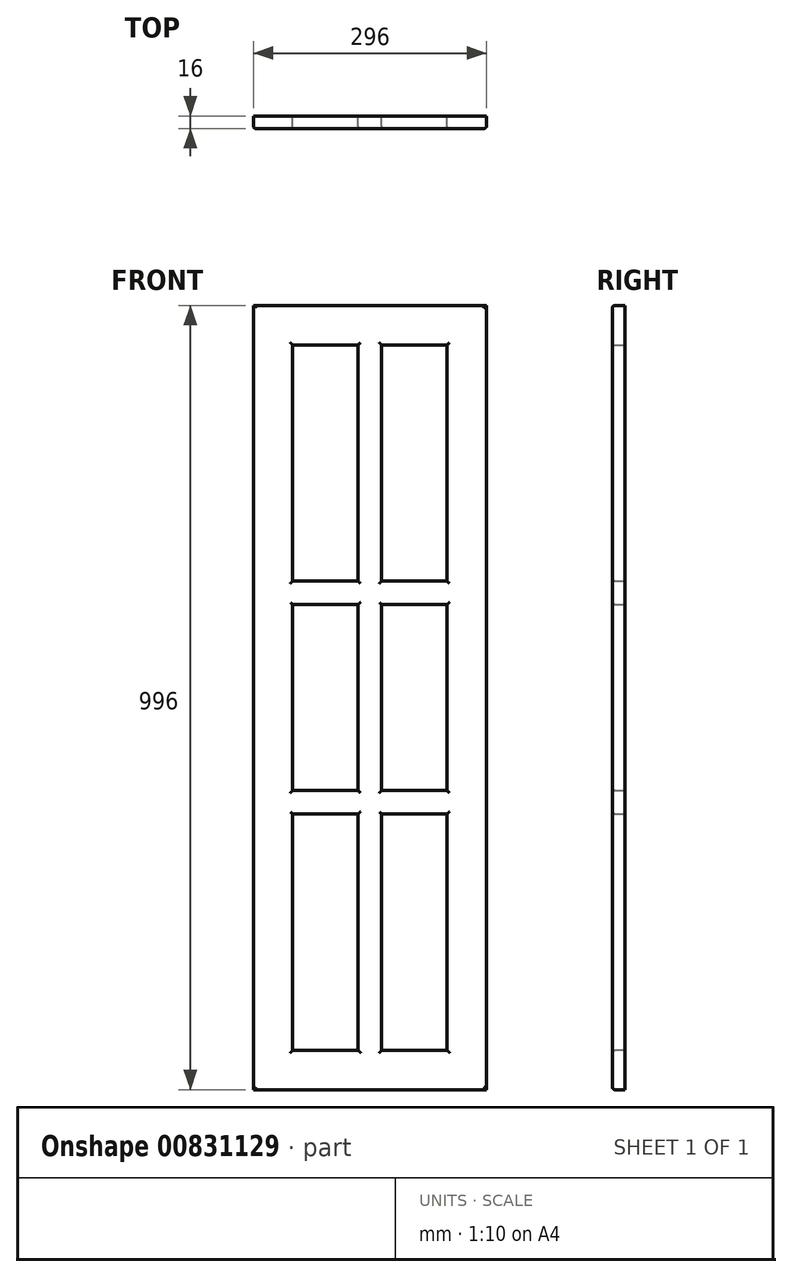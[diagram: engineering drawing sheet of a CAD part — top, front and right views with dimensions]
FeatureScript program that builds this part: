
annotation { "Feature Type Name" : "Feature", "Feature Type Description" : "" }
export const myFeature = defineFeature(function(context is Context, id is Id, definition is map)
    precondition{}
    {
        {
            var Q0;
            Q0=qCreatedBy(makeId("Front.planeOp"),FACE);
            var sketch = newSketch(context, id + "F0", { "sketchPlane" : qUnion([Q0])});
            skLineSegment(sketch, "E0.bottom", {"start": v(0, 0) * mm, "end": v(28.85, 0) * mm});
            skLineSegment(sketch, "E0.top", {"start": v(0, 37.88) * mm, "end": v(28.85, 37.88) * mm});
            skLineSegment(sketch, "E0.left", {"start": v(0, 0) * mm, "end": v(0, 37.88) * mm});
            skLineSegment(sketch, "E0.right", {"start": v(28.85, 0) * mm, "end": v(28.85, 37.88) * mm});
            skSolve(sketch);
        }
        {
            var Q0;
            Q0=makeQuery(id+"F0.imprint","IMPRINT",FACE,{"disambiguationData":[TD([[makeQuery(id+"F0.imprint","IMPRINT",EDGE,{"derivedFrom":sQuery(id+"F0.wireOp",EDGE,"E0.bottom")}),1.0]])]});
            extrude(context, id + "F1", {"entities" : qUnion([Q0]), "depth" : 16 * mm, "offsetDistance" : 25.4 * mm});
        }
        {
            var Q0;
            Q0=makeQuery(id+"F1.opExtrude","SWEPT_FACE",FACE,{"disambiguationData":[OSD([sQuery(id+"F0.wireOp",EDGE,"E0.left")])]});
            extrude(context, id + "F2", {"entities" : qUnion([Q0]), "operationType" : NewBodyOperationType.ADD, "oppositeDirection" : true, "depth" : 296 * mm, "offsetDistance" : 25.4 * mm});
        }
        {
            var Q0;
            {var subQ0=sQuery(id+"F0.wireOp",EDGE,"E0.bottom");Q0=makeQuery(id+"F2.boolean.opBoolean","MERGE",FACE,{"derivedFrom":[makeQuery(id+"F1.opExtrude","SWEPT_FACE",FACE,{"disambiguationData":[OSD([subQ0])]}),makeQuery(id+"F2.opExtrude","SWEPT_FACE",FACE,{"disambiguationData":[OSD([subQ0,sQuery(id+"F0.wireOp",EDGE,"E0.left")])]})]});}
            extrude(context, id + "F3", {"entities" : qUnion([Q0]), "operationType" : NewBodyOperationType.ADD, "oppositeDirection" : true, "depth" : 996 * mm, "offsetDistance" : 25 * mm});
        }
        {
            var Q0;
            {var subQ0=sQuery(id+"F0.wireOp",EDGE,"E0.left");var subQ1=sQuery(id+"F0.wireOp",EDGE,"E0.bottom");Q0=makeQuery(id+"F3.boolean.opBoolean","MERGE",FACE,{"derivedFrom":[makeQuery(id+"F2.boolean.opBoolean","MERGE",FACE,{"derivedFrom":[makeQuery(id+"F1.opExtrude","CAP_FACE",FACE,{"disambiguationData":[OSD([subQ1,sQuery(id+"F0.wireOp",EDGE,"E0.top"),subQ0,sQuery(id+"F0.wireOp",EDGE,"E0.right")])],"isStart":false}),makeQuery(id+"F2.opExtrude","SWEPT_FACE",FACE,{"disambiguationData":[OSD([subQ0]),TDD([makeQuery(id+"F1.opExtrude","CAP_EDGE",EDGE,{"disambiguationData":[OSD([subQ0])],"isStart":false})])]})]}),makeQuery(id+"F3.opExtrude","SWEPT_FACE",FACE,{"disambiguationData":[OSD([subQ1,subQ0]),TDD([makeQuery(id+"F2.boolean.opBoolean","MERGE",EDGE,{"derivedFrom":[makeQuery(id+"F1.opExtrude","CAP_EDGE",EDGE,{"disambiguationData":[OSD([subQ1])],"isStart":false}),makeQuery(id+"F2.opExtrude","SWEPT_EDGE",EDGE,{"disambiguationData":[OSD([subQ1,subQ0]),TDD([makeQuery(id+"F1.opExtrude","CAP_VERTEX",VERTEX,{"disambiguationData":[OSD([subQ1,subQ0])],"isStart":false})])]})]})])]})]});}
            var sketch = newSketch(context, id + "F4", { "sketchPlane" : qUnion([Q0])});
            skLineSegment(sketch, "E1.bottom", {"start": v(48.4, 906.79) * mm, "end": v(248.24, 906.79) * mm});
            skLineSegment(sketch, "E1.top", {"start": v(48.4, 105.66) * mm, "end": v(248.24, 105.66) * mm});
            skLineSegment(sketch, "E1.left", {"start": v(48.4, 906.79) * mm, "end": v(48.4, 105.66) * mm});
            skLineSegment(sketch, "E1.right", {"start": v(248.24, 906.79) * mm, "end": v(248.24, 105.66) * mm});
            skSolve(sketch);
        }
        {
            var Q0;
            Q0=makeQuery(id+"F4.imprint","IMPRINT",FACE,{"disambiguationData":[TD([[makeQuery(id+"F4.imprint","IMPRINT",EDGE,{"derivedFrom":sQuery(id+"F4.wireOp",EDGE,"E1.bottom")}),-1.0]])]});
            extrude(context, id + "F5", {"entities" : qUnion([Q0]), "operationType" : NewBodyOperationType.REMOVE, "oppositeDirection" : true, "depth" : 5 * mm, "offsetDistance" : 25 * mm});
        }
        {
            var Q0;
            Q0=makeQuery(id+"F5.boolean.opBoolean","COPY",FACE,{"derivedFrom":makeQuery(id+"F5.opExtrude","SWEPT_FACE",FACE,{"disambiguationData":[OSD([sQuery(id+"F4.wireOp",EDGE,"E1.bottom")])]})});
            extrude(context, id + "F6", {"entities" : qUnion([Q0]), "operationType" : NewBodyOperationType.REMOVE, "oppositeDirection" : true, "depth" : 39.2 * mm, "offsetDistance" : 25 * mm});
        }
        {
            var Q0;
            {var subQ0=sQuery(id+"F4.wireOp",EDGE,"E1.right");Q0=makeQuery(id+"F6.boolean.opBoolean","MERGE",FACE,{"derivedFrom":[makeQuery(id+"F5.boolean.opBoolean","COPY",FACE,{"derivedFrom":makeQuery(id+"F5.opExtrude","SWEPT_FACE",FACE,{"disambiguationData":[OSD([subQ0])]})}),makeQuery(id+"F6.opExtrude","SWEPT_FACE",FACE,{"disambiguationData":[OSD([sQuery(id+"F4.wireOp",EDGE,"E1.bottom"),subQ0])]})]});}
            extrude(context, id + "F7", {"entities" : qUnion([Q0]), "operationType" : NewBodyOperationType.ADD, "depth" : 2.24 * mm, "offsetDistance" : 25 * mm});
        }
        {
            var Q0;
            Q0=makeQuery(id+"F5.boolean.opBoolean","COPY",FACE,{"derivedFrom":makeQuery(id+"F5.opExtrude","SWEPT_FACE",FACE,{"disambiguationData":[OSD([sQuery(id+"F4.wireOp",EDGE,"E1.top")])]})});
            extrude(context, id + "F8", {"entities" : qUnion([Q0]), "operationType" : NewBodyOperationType.REMOVE, "oppositeDirection" : true, "depth" : 55.66 * mm, "offsetDistance" : 25 * mm});
        }
        {
            var Q0;
            {var subQ0=sQuery(id+"F4.wireOp",EDGE,"E1.left");Q0=makeQuery(id+"F8.boolean.opBoolean","MERGE",FACE,{"derivedFrom":[makeQuery(id+"F6.boolean.opBoolean","MERGE",FACE,{"derivedFrom":[makeQuery(id+"F5.boolean.opBoolean","COPY",FACE,{"derivedFrom":makeQuery(id+"F5.opExtrude","SWEPT_FACE",FACE,{"disambiguationData":[OSD([subQ0])]})}),makeQuery(id+"F6.opExtrude","SWEPT_FACE",FACE,{"disambiguationData":[OSD([sQuery(id+"F4.wireOp",EDGE,"E1.bottom"),subQ0])]})]}),makeQuery(id+"F8.opExtrude","SWEPT_FACE",FACE,{"disambiguationData":[OSD([sQuery(id+"F4.wireOp",EDGE,"E1.top"),subQ0])]})]});}
            extrude(context, id + "F9", {"entities" : qUnion([Q0]), "operationType" : NewBodyOperationType.ADD, "depth" : 1.59 * mm, "offsetDistance" : 25 * mm});
        }
        {
            var Q0;
            {var subQ0=sQuery(id+"F4.wireOp",EDGE,"E1.top");var subQ1=sQuery(id+"F4.wireOp",EDGE,"E1.bottom");Q0=makeQuery(id+"F8.boolean.opBoolean","MERGE",FACE,{"derivedFrom":[makeQuery(id+"F6.boolean.opBoolean","MERGE",FACE,{"derivedFrom":[makeQuery(id+"F5.boolean.opBoolean","COPY",FACE,{"derivedFrom":makeQuery(id+"F5.opExtrude","CAP_FACE",FACE,{"disambiguationData":[OSD([subQ1,subQ0,sQuery(id+"F4.wireOp",EDGE,"E1.left"),sQuery(id+"F4.wireOp",EDGE,"E1.right")])],"isStart":false})}),makeQuery(id+"F6.opExtrude","SWEPT_FACE",FACE,{"disambiguationData":[OSD([subQ1]),TDD([makeQuery(id+"F5.boolean.opBoolean","COPY",EDGE,{"derivedFrom":makeQuery(id+"F5.opExtrude","CAP_EDGE",EDGE,{"disambiguationData":[OSD([subQ1])],"isStart":false})})])]})]}),makeQuery(id+"F8.opExtrude","SWEPT_FACE",FACE,{"disambiguationData":[OSD([subQ0]),TDD([makeQuery(id+"F5.boolean.opBoolean","COPY",EDGE,{"derivedFrom":makeQuery(id+"F5.opExtrude","CAP_EDGE",EDGE,{"disambiguationData":[OSD([subQ0])],"isStart":false})})])]})]});}
            var sketch = newSketch(context, id + "F10", { "sketchPlane" : qUnion([Q0])});
            skLineSegment(sketch, "E2.bottom", {"start": v(127.14, 946) * mm, "end": v(181.91, 946) * mm});
            skLineSegment(sketch, "E2.top", {"start": v(127.14, 50) * mm, "end": v(181.91, 50) * mm});
            skLineSegment(sketch, "E2.left", {"start": v(127.14, 946) * mm, "end": v(127.14, 50) * mm});
            skLineSegment(sketch, "E2.right", {"start": v(181.91, 946) * mm, "end": v(181.91, 50) * mm});
            skSolve(sketch);
        }
        {
            var Q0;
            Q0=makeQuery(id+"F10.imprint","IMPRINT",FACE,{"disambiguationData":[TD([[makeQuery(id+"F10.imprint","IMPRINT",EDGE,{"derivedFrom":sQuery(id+"F10.wireOp",EDGE,"E2.bottom")}),-1.0]])]});
            extrude(context, id + "F11", {"entities" : qUnion([Q0]), "operationType" : NewBodyOperationType.ADD, "depth" : 5 * mm, "offsetDistance" : 25 * mm});
        }
        {
            var Q0;
            Q0=makeQuery(id+"F11.opExtrude","SWEPT_FACE",FACE,{"disambiguationData":[OSD([sQuery(id+"F10.wireOp",EDGE,"E2.left")])]});
            extrude(context, id + "F12", {"entities" : qUnion([Q0]), "operationType" : NewBodyOperationType.REMOVE, "oppositeDirection" : true, "depth" : 5.86 * mm, "offsetDistance" : 25 * mm});
        }
        {
            var Q0;
            Q0=makeQuery(id+"F11.opExtrude","SWEPT_FACE",FACE,{"disambiguationData":[OSD([sQuery(id+"F10.wireOp",EDGE,"E2.right")])]});
            extrude(context, id + "F13", {"entities" : qUnion([Q0]), "operationType" : NewBodyOperationType.REMOVE, "oppositeDirection" : true, "depth" : 18.91 * mm, "offsetDistance" : 25 * mm});
        }
        {
            var Q0;
            {var subQ0=sQuery(id+"F10.wireOp",EDGE,"E2.left");var subQ1=sQuery(id+"F4.wireOp",EDGE,"E1.bottom");var subQ2=sQuery(id+"F4.wireOp",EDGE,"E1.top");var subQ3=sQuery(id+"F4.wireOp",EDGE,"E1.left");Q0=makeQuery(id+"F12.boolean.opBoolean","MERGE",FACE,{"derivedFrom":[makeQuery(id+"F11.boolean.opBoolean","SPLIT",FACE,{"disambiguationData":[TD([makeQuery(id+"F11.opExtrude","SWEPT_FACE",FACE,{"disambiguationData":[OSD([subQ0])]})])],"derivedFrom":makeQuery(id+"F8.boolean.opBoolean","MERGE",FACE,{"derivedFrom":[makeQuery(id+"F6.boolean.opBoolean","MERGE",FACE,{"derivedFrom":[makeQuery(id+"F5.boolean.opBoolean","COPY",FACE,{"derivedFrom":makeQuery(id+"F5.opExtrude","CAP_FACE",FACE,{"disambiguationData":[OSD([subQ1,subQ2,subQ3,sQuery(id+"F4.wireOp",EDGE,"E1.right")])],"isStart":false})}),makeQuery(id+"F6.opExtrude","SWEPT_FACE",FACE,{"disambiguationData":[OSD([subQ1]),TDD([makeQuery(id+"F5.boolean.opBoolean","COPY",EDGE,{"derivedFrom":makeQuery(id+"F5.opExtrude","CAP_EDGE",EDGE,{"disambiguationData":[OSD([subQ1])],"isStart":false})})])]})]}),makeQuery(id+"F8.opExtrude","SWEPT_FACE",FACE,{"disambiguationData":[OSD([subQ2]),TDD([makeQuery(id+"F5.boolean.opBoolean","COPY",EDGE,{"derivedFrom":makeQuery(id+"F5.opExtrude","CAP_EDGE",EDGE,{"disambiguationData":[OSD([subQ2])],"isStart":false})})])]})]})}),makeQuery(id+"F12.opExtrude","SWEPT_FACE",FACE,{"disambiguationData":[OSD([subQ0]),TDD([makeQuery(id+"F11.opExtrude","CAP_EDGE",EDGE,{"disambiguationData":[OSD([subQ0])],"isStart":true})])]})]});}
            var sketch = newSketch(context, id + "F14", { "sketchPlane" : qUnion([Q0])});
            skLineSegment(sketch, "E3.bottom", {"start": v(50, 870.78) * mm, "end": v(133, 870.78) * mm});
            skLineSegment(sketch, "E3.top", {"start": v(50, 835.83) * mm, "end": v(133, 835.83) * mm});
            skLineSegment(sketch, "E3.left", {"start": v(50, 870.78) * mm, "end": v(50, 835.83) * mm});
            skLineSegment(sketch, "E3.right", {"start": v(133, 870.78) * mm, "end": v(133, 835.83) * mm});
            skLineSegment(sketch, "E4.bottom", {"start": v(50, 539.3) * mm, "end": v(133, 539.3) * mm});
            skLineSegment(sketch, "E4.top", {"start": v(50, 484.02) * mm, "end": v(133, 484.02) * mm});
            skLineSegment(sketch, "E4.left", {"start": v(50, 539.3) * mm, "end": v(50, 484.02) * mm});
            skLineSegment(sketch, "E4.right", {"start": v(133, 539.3) * mm, "end": v(133, 484.02) * mm});
            skSolve(sketch);
        }
        {
            var Q0;
            {var subQ0=sQuery(id+"F10.wireOp",EDGE,"E2.right");var subQ1=sQuery(id+"F4.wireOp",EDGE,"E1.top");var subQ2=sQuery(id+"F4.wireOp",EDGE,"E1.right");var subQ3=sQuery(id+"F4.wireOp",EDGE,"E1.bottom");Q0=makeQuery(id+"F13.boolean.opBoolean","MERGE",FACE,{"derivedFrom":[makeQuery(id+"F11.boolean.opBoolean","SPLIT",FACE,{"disambiguationData":[TD([makeQuery(id+"F11.opExtrude","SWEPT_FACE",FACE,{"disambiguationData":[OSD([subQ0])]})])],"derivedFrom":makeQuery(id+"F8.boolean.opBoolean","MERGE",FACE,{"derivedFrom":[makeQuery(id+"F6.boolean.opBoolean","MERGE",FACE,{"derivedFrom":[makeQuery(id+"F5.boolean.opBoolean","COPY",FACE,{"derivedFrom":makeQuery(id+"F5.opExtrude","CAP_FACE",FACE,{"disambiguationData":[OSD([subQ3,subQ1,sQuery(id+"F4.wireOp",EDGE,"E1.left"),subQ2])],"isStart":false})}),makeQuery(id+"F6.opExtrude","SWEPT_FACE",FACE,{"disambiguationData":[OSD([subQ3]),TDD([makeQuery(id+"F5.boolean.opBoolean","COPY",EDGE,{"derivedFrom":makeQuery(id+"F5.opExtrude","CAP_EDGE",EDGE,{"disambiguationData":[OSD([subQ3])],"isStart":false})})])]})]}),makeQuery(id+"F8.opExtrude","SWEPT_FACE",FACE,{"disambiguationData":[OSD([subQ1]),TDD([makeQuery(id+"F5.boolean.opBoolean","COPY",EDGE,{"derivedFrom":makeQuery(id+"F5.opExtrude","CAP_EDGE",EDGE,{"disambiguationData":[OSD([subQ1])],"isStart":false})})])]})]})}),makeQuery(id+"F13.opExtrude","SWEPT_FACE",FACE,{"disambiguationData":[OSD([subQ0]),TDD([makeQuery(id+"F11.opExtrude","CAP_EDGE",EDGE,{"disambiguationData":[OSD([subQ0])],"isStart":true})])]})]});}
            var sketch = newSketch(context, id + "F15", { "sketchPlane" : qUnion([Q0])});
            skLineSegment(sketch, "E5.bottom", {"start": v(163, 876.14) * mm, "end": v(246, 876.14) * mm});
            skLineSegment(sketch, "E5.top", {"start": v(163, 831.26) * mm, "end": v(246, 831.26) * mm});
            skLineSegment(sketch, "E5.left", {"start": v(163, 876.14) * mm, "end": v(163, 831.26) * mm});
            skLineSegment(sketch, "E5.right", {"start": v(246, 876.14) * mm, "end": v(246, 831.26) * mm});
            skLineSegment(sketch, "E6.bottom", {"start": v(163, 602.8) * mm, "end": v(246, 602.8) * mm});
            skLineSegment(sketch, "E6.top", {"start": v(163, 550.28) * mm, "end": v(246, 550.28) * mm});
            skLineSegment(sketch, "E6.left", {"start": v(163, 602.8) * mm, "end": v(163, 550.28) * mm});
            skLineSegment(sketch, "E6.right", {"start": v(246, 602.8) * mm, "end": v(246, 550.28) * mm});
            skSolve(sketch);
        }
        {
            var Q0;
            Q0=makeQuery(id+"F14.imprint","IMPRINT",FACE,{"disambiguationData":[TD([[makeQuery(id+"F14.imprint","IMPRINT",EDGE,{"derivedFrom":sQuery(id+"F14.wireOp",EDGE,"E3.bottom")}),-1.0]])]});
            var Q1;
            Q1=makeQuery(id+"F15.imprint","IMPRINT",FACE,{"disambiguationData":[TD([[makeQuery(id+"F15.imprint","IMPRINT",EDGE,{"derivedFrom":sQuery(id+"F15.wireOp",EDGE,"E5.bottom")}),-1.0]])]});
            var Q2;
            Q2=makeQuery(id+"F15.imprint","IMPRINT",FACE,{"disambiguationData":[TD([[makeQuery(id+"F15.imprint","IMPRINT",EDGE,{"derivedFrom":sQuery(id+"F15.wireOp",EDGE,"E6.bottom")}),-1.0]])]});
            var Q3;
            Q3=makeQuery(id+"F14.imprint","IMPRINT",FACE,{"disambiguationData":[TD([[makeQuery(id+"F14.imprint","IMPRINT",EDGE,{"derivedFrom":sQuery(id+"F14.wireOp",EDGE,"E4.bottom")}),-1.0]])]});
            extrude(context, id + "F16", {"entities" : qUnion([Q0, Q1, Q2, Q3]), "operationType" : NewBodyOperationType.ADD, "depth" : 5 * mm, "offsetDistance" : 25 * mm});
        }
        {
            var Q0;
            Q0=makeQuery(id+"F16.opExtrude","SWEPT_FACE",FACE,{"disambiguationData":[OSD([sQuery(id+"F15.wireOp",EDGE,"E6.top")])]});
            var Q1;
            Q1=makeQuery(id+"F16.opExtrude","SWEPT_FACE",FACE,{"disambiguationData":[OSD([sQuery(id+"F14.wireOp",EDGE,"E4.top")])]});
            extrude(context, id + "F17", {"entities" : qUnion([Q0, Q1]), "operationType" : NewBodyOperationType.ADD, "depth" : 300 * mm, "offsetDistance" : 25 * mm});
        }
        {
            var Q0;
            Q0=makeQuery(id+"F16.opExtrude","SWEPT_FACE",FACE,{"disambiguationData":[OSD([sQuery(id+"F14.wireOp",EDGE,"E4.bottom")])]});
            var Q1;
            Q1=makeQuery(id+"F16.opExtrude","SWEPT_FACE",FACE,{"disambiguationData":[OSD([sQuery(id+"F15.wireOp",EDGE,"E6.bottom")])]});
            extrude(context, id + "F18", {"entities" : qUnion([Q0, Q1]), "operationType" : NewBodyOperationType.REMOVE, "oppositeDirection" : true, "depth" : 300 * mm, "offsetDistance" : 25 * mm});
        }
        {
            var Q0;
            Q0=makeQuery(id+"F16.opExtrude","SWEPT_FACE",FACE,{"disambiguationData":[OSD([sQuery(id+"F14.wireOp",EDGE,"E3.top")])]});
            extrude(context, id + "F19", {"entities" : qUnion([Q0]), "operationType" : NewBodyOperationType.ADD, "depth" : 324.8 * mm, "offsetDistance" : 25 * mm});
        }
        {
            var Q0;
            Q0=makeQuery(id+"F16.opExtrude","SWEPT_FACE",FACE,{"disambiguationData":[OSD([sQuery(id+"F14.wireOp",EDGE,"E3.bottom")])]});
            extrude(context, id + "F20", {"entities" : qUnion([Q0]), "operationType" : NewBodyOperationType.REMOVE, "oppositeDirection" : true, "depth" : 324.8 * mm, "offsetDistance" : 25 * mm});
        }
        {
            var Q0;
            Q0=makeQuery(id+"F18.boolean.opBoolean","COPY",FACE,{"derivedFrom":makeQuery(id+"F18.opExtrude","CAP_FACE",FACE,{"disambiguationData":[OSD([sQuery(id+"F14.wireOp",EDGE,"E4.bottom")])],"isStart":false})});
            extrude(context, id + "F21", {"entities" : qUnion([Q0]), "operationType" : NewBodyOperationType.ADD, "depth" : 250 * mm, "offsetDistance" : 25 * mm});
        }
        {
            var Q0;
            Q0=makeQuery(id+"F17.opExtrude","CAP_FACE",FACE,{"disambiguationData":[OSD([sQuery(id+"F14.wireOp",EDGE,"E4.top")])],"isStart":false});
            extrude(context, id + "F22", {"entities" : qUnion([Q0]), "operationType" : NewBodyOperationType.REMOVE, "oppositeDirection" : true, "depth" : 250 * mm, "offsetDistance" : 25 * mm});
        }
        {
            var Q0;
            Q0=makeQuery(id+"F20.boolean.opBoolean","COPY",FACE,{"derivedFrom":makeQuery(id+"F20.opExtrude","CAP_FACE",FACE,{"disambiguationData":[OSD([sQuery(id+"F14.wireOp",EDGE,"E3.bottom")])],"isStart":false})});
            extrude(context, id + "F23", {"entities" : qUnion([Q0]), "operationType" : NewBodyOperationType.ADD, "depth" : 100 * mm, "offsetDistance" : 25 * mm});
        }
        {
            var Q0;
            Q0=makeQuery(id+"F19.opExtrude","CAP_FACE",FACE,{"disambiguationData":[OSD([sQuery(id+"F14.wireOp",EDGE,"E3.top")])],"isStart":false});
            extrude(context, id + "F24", {"entities" : qUnion([Q0]), "operationType" : NewBodyOperationType.REMOVE, "oppositeDirection" : true, "depth" : 100 * mm, "offsetDistance" : 25 * mm});
        }
        {
            var Q0;
            Q0=makeQuery(id+"F23.opExtrude","CAP_FACE",FACE,{"disambiguationData":[OSD([sQuery(id+"F14.wireOp",EDGE,"E3.bottom")])],"isStart":false});
            extrude(context, id + "F25", {"entities" : qUnion([Q0]), "operationType" : NewBodyOperationType.ADD, "depth" : 50 * mm, "offsetDistance" : 25 * mm});
        }
        {
            var Q0;
            Q0=makeQuery(id+"F24.boolean.opBoolean","COPY",FACE,{"derivedFrom":makeQuery(id+"F24.opExtrude","CAP_FACE",FACE,{"disambiguationData":[OSD([sQuery(id+"F14.wireOp",EDGE,"E3.top")])],"isStart":false})});
            extrude(context, id + "F26", {"entities" : qUnion([Q0]), "operationType" : NewBodyOperationType.REMOVE, "oppositeDirection" : true, "depth" : 50 * mm, "offsetDistance" : 25 * mm});
        }
        {
            var Q0;
            Q0=makeQuery(id+"F22.boolean.opBoolean","COPY",FACE,{"derivedFrom":makeQuery(id+"F22.opExtrude","CAP_FACE",FACE,{"disambiguationData":[OSD([sQuery(id+"F14.wireOp",EDGE,"E4.top")])],"isStart":false})});
            extrude(context, id + "F27", {"entities" : qUnion([Q0]), "operationType" : NewBodyOperationType.ADD, "depth" : 134.02 * mm, "offsetDistance" : 25 * mm});
        }
        {
            var Q0;
            Q0=makeQuery(id+"F27.opExtrude","CAP_FACE",FACE,{"disambiguationData":[OSD([sQuery(id+"F14.wireOp",EDGE,"E4.top")])],"isStart":false});
            extrude(context, id + "F28", {"entities" : qUnion([Q0]), "operationType" : NewBodyOperationType.REMOVE, "oppositeDirection" : true, "depth" : 100 * mm, "offsetDistance" : 25 * mm});
        }
        {
            var Q0;
            Q0=makeQuery(id+"F26.boolean.opBoolean","COPY",FACE,{"derivedFrom":makeQuery(id+"F26.opExtrude","CAP_FACE",FACE,{"disambiguationData":[OSD([sQuery(id+"F14.wireOp",EDGE,"E3.top")])],"isStart":false})});
            extrude(context, id + "F29", {"entities" : qUnion([Q0]), "operationType" : NewBodyOperationType.ADD, "depth" : 100 * mm, "offsetDistance" : 25 * mm});
        }
        {
            var Q0;
            Q0=makeQuery(id+"F25.opExtrude","CAP_FACE",FACE,{"disambiguationData":[OSD([sQuery(id+"F14.wireOp",EDGE,"E3.bottom")])],"isStart":false});
            extrude(context, id + "F30", {"entities" : qUnion([Q0]), "operationType" : NewBodyOperationType.REMOVE, "oppositeDirection" : true, "depth" : 100 * mm, "offsetDistance" : 25 * mm});
        }
        {
            var Q0;
            Q0=makeQuery(id+"F30.boolean.opBoolean","COPY",FACE,{"derivedFrom":makeQuery(id+"F30.opExtrude","CAP_FACE",FACE,{"disambiguationData":[OSD([sQuery(id+"F14.wireOp",EDGE,"E3.bottom")])],"isStart":false})});
            extrude(context, id + "F31", {"entities" : qUnion([Q0]), "operationType" : NewBodyOperationType.ADD, "depth" : 50 * mm, "offsetDistance" : 25 * mm});
        }
        {
            var Q0;
            Q0=makeQuery(id+"F29.opExtrude","CAP_FACE",FACE,{"disambiguationData":[OSD([sQuery(id+"F14.wireOp",EDGE,"E3.top")])],"isStart":false});
            extrude(context, id + "F32", {"entities" : qUnion([Q0]), "operationType" : NewBodyOperationType.REMOVE, "oppositeDirection" : true, "depth" : 54.95 * mm, "offsetDistance" : 25 * mm});
        }
        {
            var Q0;
            Q0=makeQuery(id+"F28.boolean.opBoolean","COPY",FACE,{"derivedFrom":makeQuery(id+"F28.opExtrude","CAP_FACE",FACE,{"disambiguationData":[OSD([sQuery(id+"F14.wireOp",EDGE,"E4.top")])],"isStart":false})});
            extrude(context, id + "F33", {"entities" : qUnion([Q0]), "operationType" : NewBodyOperationType.ADD, "depth" : 50 * mm, "offsetDistance" : 25 * mm});
        }
        {
            var Q0;
            Q0=makeQuery(id+"F21.opExtrude","CAP_FACE",FACE,{"disambiguationData":[OSD([sQuery(id+"F14.wireOp",EDGE,"E4.bottom")])],"isStart":false});
            extrude(context, id + "F34", {"entities" : qUnion([Q0]), "operationType" : NewBodyOperationType.REMOVE, "oppositeDirection" : true, "depth" : 109.3 * mm, "offsetDistance" : 25 * mm});
        }
        {
            var Q0;
            Q0=makeQuery(id+"F16.opExtrude","SWEPT_FACE",FACE,{"disambiguationData":[OSD([sQuery(id+"F15.wireOp",EDGE,"E5.top")])]});
            extrude(context, id + "F35", {"entities" : qUnion([Q0]), "operationType" : NewBodyOperationType.REMOVE, "oppositeDirection" : true, "depth" : 14.88 * mm, "offsetDistance" : 25 * mm});
        }
        {
            var Q0;
            Q0=makeQuery(id+"F35.boolean.opBoolean","COPY",FACE,{"derivedFrom":makeQuery(id+"F35.opExtrude","CAP_FACE",FACE,{"disambiguationData":[OSD([sQuery(id+"F15.wireOp",EDGE,"E5.top")])],"isStart":false})});
            extrude(context, id + "F36", {"entities" : qUnion([Q0]), "operationType" : NewBodyOperationType.ADD, "depth" : 230.15 * mm, "offsetDistance" : 25 * mm});
        }
        {
            var Q0;
            Q0=makeQuery(id+"F16.opExtrude","SWEPT_FACE",FACE,{"disambiguationData":[OSD([sQuery(id+"F15.wireOp",EDGE,"E5.bottom")])]});
            extrude(context, id + "F37", {"entities" : qUnion([Q0]), "operationType" : NewBodyOperationType.REMOVE, "oppositeDirection" : true, "depth" : 230.15 * mm, "offsetDistance" : 25 * mm});
        }
        {
            var Q0;
            Q0=makeQuery(id+"F17.opExtrude","CAP_FACE",FACE,{"disambiguationData":[OSD([sQuery(id+"F15.wireOp",EDGE,"E6.top")])],"isStart":false});
            extrude(context, id + "F38", {"entities" : qUnion([Q0]), "operationType" : NewBodyOperationType.REMOVE, "oppositeDirection" : true, "depth" : 22.52 * mm, "offsetDistance" : 25 * mm});
        }
        {
            var Q0;
            Q0=makeQuery(id+"F18.boolean.opBoolean","COPY",FACE,{"derivedFrom":makeQuery(id+"F18.opExtrude","CAP_FACE",FACE,{"disambiguationData":[OSD([sQuery(id+"F15.wireOp",EDGE,"E6.bottom")])],"isStart":false})});
            extrude(context, id + "F39", {"entities" : qUnion([Q0]), "operationType" : NewBodyOperationType.ADD, "depth" : 77.2 * mm, "offsetDistance" : 25 * mm});
        }
        {
            var Q0;
            Q0=makeQuery(id+"F38.boolean.opBoolean","COPY",FACE,{"derivedFrom":makeQuery(id+"F38.opExtrude","CAP_FACE",FACE,{"disambiguationData":[OSD([sQuery(id+"F15.wireOp",EDGE,"E6.top")])],"isStart":false})});
            extrude(context, id + "F40", {"entities" : qUnion([Q0]), "operationType" : NewBodyOperationType.REMOVE, "oppositeDirection" : true, "depth" : 77.2 * mm, "offsetDistance" : 25 * mm});
        }
        {
            var Q0;
            {var subQ0=sQuery(id+"F14.wireOp",EDGE,"E3.bottom");var subQ1=makeQuery(id+"F16.opExtrude","CAP_EDGE",EDGE,{"disambiguationData":[OSD([subQ0])],"isStart":true});var subQ2=sQuery(id+"F10.wireOp",EDGE,"E2.left");var subQ3=sQuery(id+"F4.wireOp",EDGE,"E1.bottom");var subQ4=sQuery(id+"F4.wireOp",EDGE,"E1.left");var subQ5=sQuery(id+"F4.wireOp",EDGE,"E1.top");var subQ7=makeQuery(id+"F6.boolean.opBoolean","COPY",FACE,{"derivedFrom":makeQuery(id+"F6.opExtrude","CAP_FACE",FACE,{"disambiguationData":[OSD([subQ3])],"isStart":false})});Q0=makeQuery(id+"F30.boolean.opBoolean","MERGE",FACE,{"derivedFrom":[makeQuery(id+"F20.boolean.opBoolean","MERGE",FACE,{"derivedFrom":[makeQuery(id+"F16.boolean.opBoolean","SPLIT",FACE,{"disambiguationData":[TD([subQ7])],"derivedFrom":makeQuery(id+"F12.boolean.opBoolean","MERGE",FACE,{"derivedFrom":[makeQuery(id+"F11.boolean.opBoolean","SPLIT",FACE,{"disambiguationData":[TD([makeQuery(id+"F11.opExtrude","SWEPT_FACE",FACE,{"disambiguationData":[OSD([subQ2])]})])],"derivedFrom":makeQuery(id+"F8.boolean.opBoolean","MERGE",FACE,{"derivedFrom":[makeQuery(id+"F6.boolean.opBoolean","MERGE",FACE,{"derivedFrom":[makeQuery(id+"F5.boolean.opBoolean","COPY",FACE,{"derivedFrom":makeQuery(id+"F5.opExtrude","CAP_FACE",FACE,{"disambiguationData":[OSD([subQ3,subQ5,subQ4,sQuery(id+"F4.wireOp",EDGE,"E1.right")])],"isStart":false})}),makeQuery(id+"F6.opExtrude","SWEPT_FACE",FACE,{"disambiguationData":[OSD([subQ3]),TDD([makeQuery(id+"F5.boolean.opBoolean","COPY",EDGE,{"derivedFrom":makeQuery(id+"F5.opExtrude","CAP_EDGE",EDGE,{"disambiguationData":[OSD([subQ3])],"isStart":false})})])]})]}),makeQuery(id+"F8.opExtrude","SWEPT_FACE",FACE,{"disambiguationData":[OSD([subQ5]),TDD([makeQuery(id+"F5.boolean.opBoolean","COPY",EDGE,{"derivedFrom":makeQuery(id+"F5.opExtrude","CAP_EDGE",EDGE,{"disambiguationData":[OSD([subQ5])],"isStart":false})})])]})]})}),makeQuery(id+"F12.opExtrude","SWEPT_FACE",FACE,{"disambiguationData":[OSD([subQ2]),TDD([makeQuery(id+"F11.opExtrude","CAP_EDGE",EDGE,{"disambiguationData":[OSD([subQ2])],"isStart":true})])]})]})}),makeQuery(id+"F20.opExtrude","SWEPT_FACE",FACE,{"disambiguationData":[OSD([subQ0]),TDD([subQ1])]})]}),makeQuery(id+"F30.opExtrude","SWEPT_FACE",FACE,{"disambiguationData":[OSD([subQ0]),TDD([makeQuery(id+"F25.opExtrude","CAP_EDGE",EDGE,{"disambiguationData":[OSD([subQ0]),TDD([makeQuery(id+"F23.opExtrude","CAP_EDGE",EDGE,{"disambiguationData":[OSD([subQ0]),TDD([makeQuery(id+"F20.boolean.opBoolean","COPY",EDGE,{"derivedFrom":makeQuery(id+"F20.opExtrude","CAP_EDGE",EDGE,{"disambiguationData":[OSD([subQ0]),TDD([subQ1])],"isStart":false})})])],"isStart":false})])],"isStart":false})])]})]});}
            var Q1;
            {var subQ0=sQuery(id+"F15.wireOp",EDGE,"E5.bottom");var subQ1=sQuery(id+"F10.wireOp",EDGE,"E2.right");var subQ2=sQuery(id+"F4.wireOp",EDGE,"E1.bottom");var subQ3=sQuery(id+"F4.wireOp",EDGE,"E1.right");var subQ4=sQuery(id+"F4.wireOp",EDGE,"E1.top");var subQ7=makeQuery(id+"F6.boolean.opBoolean","COPY",FACE,{"derivedFrom":makeQuery(id+"F6.opExtrude","CAP_FACE",FACE,{"disambiguationData":[OSD([subQ2])],"isStart":false})});Q1=makeQuery(id+"F37.boolean.opBoolean","MERGE",FACE,{"derivedFrom":[makeQuery(id+"F16.boolean.opBoolean","SPLIT",FACE,{"disambiguationData":[TD([subQ7])],"derivedFrom":makeQuery(id+"F13.boolean.opBoolean","MERGE",FACE,{"derivedFrom":[makeQuery(id+"F11.boolean.opBoolean","SPLIT",FACE,{"disambiguationData":[TD([makeQuery(id+"F11.opExtrude","SWEPT_FACE",FACE,{"disambiguationData":[OSD([subQ1])]})])],"derivedFrom":makeQuery(id+"F8.boolean.opBoolean","MERGE",FACE,{"derivedFrom":[makeQuery(id+"F6.boolean.opBoolean","MERGE",FACE,{"derivedFrom":[makeQuery(id+"F5.boolean.opBoolean","COPY",FACE,{"derivedFrom":makeQuery(id+"F5.opExtrude","CAP_FACE",FACE,{"disambiguationData":[OSD([subQ2,subQ4,sQuery(id+"F4.wireOp",EDGE,"E1.left"),subQ3])],"isStart":false})}),makeQuery(id+"F6.opExtrude","SWEPT_FACE",FACE,{"disambiguationData":[OSD([subQ2]),TDD([makeQuery(id+"F5.boolean.opBoolean","COPY",EDGE,{"derivedFrom":makeQuery(id+"F5.opExtrude","CAP_EDGE",EDGE,{"disambiguationData":[OSD([subQ2])],"isStart":false})})])]})]}),makeQuery(id+"F8.opExtrude","SWEPT_FACE",FACE,{"disambiguationData":[OSD([subQ4]),TDD([makeQuery(id+"F5.boolean.opBoolean","COPY",EDGE,{"derivedFrom":makeQuery(id+"F5.opExtrude","CAP_EDGE",EDGE,{"disambiguationData":[OSD([subQ4])],"isStart":false})})])]})]})}),makeQuery(id+"F13.opExtrude","SWEPT_FACE",FACE,{"disambiguationData":[OSD([subQ1]),TDD([makeQuery(id+"F11.opExtrude","CAP_EDGE",EDGE,{"disambiguationData":[OSD([subQ1])],"isStart":true})])]})]})}),makeQuery(id+"F37.opExtrude","SWEPT_FACE",FACE,{"disambiguationData":[OSD([subQ0]),TDD([makeQuery(id+"F16.opExtrude","CAP_EDGE",EDGE,{"disambiguationData":[OSD([subQ0])],"isStart":true})])]})]});}
            var Q2;
            {var subQ0=sQuery(id+"F15.wireOp",EDGE,"E5.top");var subQ1=sQuery(id+"F15.wireOp",EDGE,"E6.bottom");var subQ2=sQuery(id+"F10.wireOp",EDGE,"E2.right");var subQ3=sQuery(id+"F4.wireOp",EDGE,"E1.right");var subQ4=sQuery(id+"F4.wireOp",EDGE,"E1.top");var subQ6=sQuery(id+"F4.wireOp",EDGE,"E1.bottom");Q2=makeQuery(id+"F35.boolean.opBoolean","MERGE",FACE,{"derivedFrom":[makeQuery(id+"F18.boolean.opBoolean","MERGE",FACE,{"derivedFrom":[makeQuery(id+"F16.boolean.opBoolean","SPLIT",FACE,{"disambiguationData":[TD([makeQuery(id+"F16.opExtrude","SWEPT_FACE",FACE,{"disambiguationData":[OSD([subQ0])]})])],"derivedFrom":makeQuery(id+"F13.boolean.opBoolean","MERGE",FACE,{"derivedFrom":[makeQuery(id+"F11.boolean.opBoolean","SPLIT",FACE,{"disambiguationData":[TD([makeQuery(id+"F11.opExtrude","SWEPT_FACE",FACE,{"disambiguationData":[OSD([subQ2])]})])],"derivedFrom":makeQuery(id+"F8.boolean.opBoolean","MERGE",FACE,{"derivedFrom":[makeQuery(id+"F6.boolean.opBoolean","MERGE",FACE,{"derivedFrom":[makeQuery(id+"F5.boolean.opBoolean","COPY",FACE,{"derivedFrom":makeQuery(id+"F5.opExtrude","CAP_FACE",FACE,{"disambiguationData":[OSD([subQ6,subQ4,sQuery(id+"F4.wireOp",EDGE,"E1.left"),subQ3])],"isStart":false})}),makeQuery(id+"F6.opExtrude","SWEPT_FACE",FACE,{"disambiguationData":[OSD([subQ6]),TDD([makeQuery(id+"F5.boolean.opBoolean","COPY",EDGE,{"derivedFrom":makeQuery(id+"F5.opExtrude","CAP_EDGE",EDGE,{"disambiguationData":[OSD([subQ6])],"isStart":false})})])]})]}),makeQuery(id+"F8.opExtrude","SWEPT_FACE",FACE,{"disambiguationData":[OSD([subQ4]),TDD([makeQuery(id+"F5.boolean.opBoolean","COPY",EDGE,{"derivedFrom":makeQuery(id+"F5.opExtrude","CAP_EDGE",EDGE,{"disambiguationData":[OSD([subQ4])],"isStart":false})})])]})]})}),makeQuery(id+"F13.opExtrude","SWEPT_FACE",FACE,{"disambiguationData":[OSD([subQ2]),TDD([makeQuery(id+"F11.opExtrude","CAP_EDGE",EDGE,{"disambiguationData":[OSD([subQ2])],"isStart":true})])]})]})}),makeQuery(id+"F18.opExtrude","SWEPT_FACE",FACE,{"disambiguationData":[OSD([subQ1]),TDD([makeQuery(id+"F16.opExtrude","CAP_EDGE",EDGE,{"disambiguationData":[OSD([subQ1])],"isStart":true})])]})]}),makeQuery(id+"F35.opExtrude","SWEPT_FACE",FACE,{"disambiguationData":[OSD([subQ0]),TDD([makeQuery(id+"F16.opExtrude","CAP_EDGE",EDGE,{"disambiguationData":[OSD([subQ0])],"isStart":true})])]})]});}
            var Q3;
            {var subQ0=sQuery(id+"F14.wireOp",EDGE,"E4.bottom");var subQ1=makeQuery(id+"F16.opExtrude","CAP_EDGE",EDGE,{"disambiguationData":[OSD([subQ0])],"isStart":true});var subQ2=sQuery(id+"F14.wireOp",EDGE,"E3.top");var subQ3=makeQuery(id+"F19.opExtrude","CAP_EDGE",EDGE,{"disambiguationData":[OSD([subQ2]),TDD([makeQuery(id+"F16.opExtrude","CAP_EDGE",EDGE,{"disambiguationData":[OSD([subQ2])],"isStart":true})])],"isStart":false});var subQ4=makeQuery(id+"F24.boolean.opBoolean","COPY",EDGE,{"derivedFrom":makeQuery(id+"F24.opExtrude","CAP_EDGE",EDGE,{"disambiguationData":[OSD([subQ2]),TDD([subQ3])],"isStart":false})});var subQ5=sQuery(id+"F4.wireOp",EDGE,"E1.left");var subQ6=sQuery(id+"F4.wireOp",EDGE,"E1.top");var subQ7=sQuery(id+"F4.wireOp",EDGE,"E1.bottom");var subQ9=sQuery(id+"F10.wireOp",EDGE,"E2.left");Q3=makeQuery(id+"F34.boolean.opBoolean","MERGE",FACE,{"derivedFrom":[makeQuery(id+"F32.boolean.opBoolean","MERGE",FACE,{"derivedFrom":[makeQuery(id+"F26.boolean.opBoolean","MERGE",FACE,{"derivedFrom":[makeQuery(id+"F24.boolean.opBoolean","MERGE",FACE,{"derivedFrom":[makeQuery(id+"F18.boolean.opBoolean","MERGE",FACE,{"derivedFrom":[makeQuery(id+"F16.boolean.opBoolean","SPLIT",FACE,{"disambiguationData":[TD([makeQuery(id+"F16.opExtrude","SWEPT_FACE",FACE,{"disambiguationData":[OSD([subQ2])]})])],"derivedFrom":makeQuery(id+"F12.boolean.opBoolean","MERGE",FACE,{"derivedFrom":[makeQuery(id+"F11.boolean.opBoolean","SPLIT",FACE,{"disambiguationData":[TD([makeQuery(id+"F11.opExtrude","SWEPT_FACE",FACE,{"disambiguationData":[OSD([subQ9])]})])],"derivedFrom":makeQuery(id+"F8.boolean.opBoolean","MERGE",FACE,{"derivedFrom":[makeQuery(id+"F6.boolean.opBoolean","MERGE",FACE,{"derivedFrom":[makeQuery(id+"F5.boolean.opBoolean","COPY",FACE,{"derivedFrom":makeQuery(id+"F5.opExtrude","CAP_FACE",FACE,{"disambiguationData":[OSD([subQ7,subQ6,subQ5,sQuery(id+"F4.wireOp",EDGE,"E1.right")])],"isStart":false})}),makeQuery(id+"F6.opExtrude","SWEPT_FACE",FACE,{"disambiguationData":[OSD([subQ7]),TDD([makeQuery(id+"F5.boolean.opBoolean","COPY",EDGE,{"derivedFrom":makeQuery(id+"F5.opExtrude","CAP_EDGE",EDGE,{"disambiguationData":[OSD([subQ7])],"isStart":false})})])]})]}),makeQuery(id+"F8.opExtrude","SWEPT_FACE",FACE,{"disambiguationData":[OSD([subQ6]),TDD([makeQuery(id+"F5.boolean.opBoolean","COPY",EDGE,{"derivedFrom":makeQuery(id+"F5.opExtrude","CAP_EDGE",EDGE,{"disambiguationData":[OSD([subQ6])],"isStart":false})})])]})]})}),makeQuery(id+"F12.opExtrude","SWEPT_FACE",FACE,{"disambiguationData":[OSD([subQ9]),TDD([makeQuery(id+"F11.opExtrude","CAP_EDGE",EDGE,{"disambiguationData":[OSD([subQ9])],"isStart":true})])]})]})}),makeQuery(id+"F18.opExtrude","SWEPT_FACE",FACE,{"disambiguationData":[OSD([subQ0]),TDD([subQ1])]})]}),makeQuery(id+"F24.opExtrude","SWEPT_FACE",FACE,{"disambiguationData":[OSD([subQ2]),TDD([subQ3])]})]}),makeQuery(id+"F26.opExtrude","SWEPT_FACE",FACE,{"disambiguationData":[OSD([subQ2]),TDD([subQ4])]})]}),makeQuery(id+"F32.opExtrude","SWEPT_FACE",FACE,{"disambiguationData":[OSD([subQ2]),TDD([makeQuery(id+"F29.opExtrude","CAP_EDGE",EDGE,{"disambiguationData":[OSD([subQ2]),TDD([makeQuery(id+"F26.boolean.opBoolean","COPY",EDGE,{"derivedFrom":makeQuery(id+"F26.opExtrude","CAP_EDGE",EDGE,{"disambiguationData":[OSD([subQ2]),TDD([subQ4])],"isStart":false})})])],"isStart":false})])]})]}),makeQuery(id+"F34.opExtrude","SWEPT_FACE",FACE,{"disambiguationData":[OSD([subQ0]),TDD([makeQuery(id+"F21.opExtrude","CAP_EDGE",EDGE,{"disambiguationData":[OSD([subQ0]),TDD([makeQuery(id+"F18.boolean.opBoolean","COPY",EDGE,{"derivedFrom":makeQuery(id+"F18.opExtrude","CAP_EDGE",EDGE,{"disambiguationData":[OSD([subQ0]),TDD([subQ1])],"isStart":false})})])],"isStart":false})])]})]});}
            var Q4;
            {var subQ0=sQuery(id+"F14.wireOp",EDGE,"E4.top");var subQ1=makeQuery(id+"F17.opExtrude","CAP_EDGE",EDGE,{"disambiguationData":[OSD([subQ0]),TDD([makeQuery(id+"F16.opExtrude","CAP_EDGE",EDGE,{"disambiguationData":[OSD([subQ0])],"isStart":true})])],"isStart":false});var subQ2=sQuery(id+"F10.wireOp",EDGE,"E2.left");var subQ3=sQuery(id+"F4.wireOp",EDGE,"E1.top");var subQ4=sQuery(id+"F4.wireOp",EDGE,"E1.left");var subQ5=sQuery(id+"F4.wireOp",EDGE,"E1.bottom");var subQ7=makeQuery(id+"F8.boolean.opBoolean","COPY",FACE,{"derivedFrom":makeQuery(id+"F8.opExtrude","CAP_FACE",FACE,{"disambiguationData":[OSD([subQ3])],"isStart":false})});Q4=makeQuery(id+"F28.boolean.opBoolean","MERGE",FACE,{"derivedFrom":[makeQuery(id+"F22.boolean.opBoolean","MERGE",FACE,{"derivedFrom":[makeQuery(id+"F16.boolean.opBoolean","SPLIT",FACE,{"disambiguationData":[TD([subQ7])],"derivedFrom":makeQuery(id+"F12.boolean.opBoolean","MERGE",FACE,{"derivedFrom":[makeQuery(id+"F11.boolean.opBoolean","SPLIT",FACE,{"disambiguationData":[TD([makeQuery(id+"F11.opExtrude","SWEPT_FACE",FACE,{"disambiguationData":[OSD([subQ2])]})])],"derivedFrom":makeQuery(id+"F8.boolean.opBoolean","MERGE",FACE,{"derivedFrom":[makeQuery(id+"F6.boolean.opBoolean","MERGE",FACE,{"derivedFrom":[makeQuery(id+"F5.boolean.opBoolean","COPY",FACE,{"derivedFrom":makeQuery(id+"F5.opExtrude","CAP_FACE",FACE,{"disambiguationData":[OSD([subQ5,subQ3,subQ4,sQuery(id+"F4.wireOp",EDGE,"E1.right")])],"isStart":false})}),makeQuery(id+"F6.opExtrude","SWEPT_FACE",FACE,{"disambiguationData":[OSD([subQ5]),TDD([makeQuery(id+"F5.boolean.opBoolean","COPY",EDGE,{"derivedFrom":makeQuery(id+"F5.opExtrude","CAP_EDGE",EDGE,{"disambiguationData":[OSD([subQ5])],"isStart":false})})])]})]}),makeQuery(id+"F8.opExtrude","SWEPT_FACE",FACE,{"disambiguationData":[OSD([subQ3]),TDD([makeQuery(id+"F5.boolean.opBoolean","COPY",EDGE,{"derivedFrom":makeQuery(id+"F5.opExtrude","CAP_EDGE",EDGE,{"disambiguationData":[OSD([subQ3])],"isStart":false})})])]})]})}),makeQuery(id+"F12.opExtrude","SWEPT_FACE",FACE,{"disambiguationData":[OSD([subQ2]),TDD([makeQuery(id+"F11.opExtrude","CAP_EDGE",EDGE,{"disambiguationData":[OSD([subQ2])],"isStart":true})])]})]})}),makeQuery(id+"F22.opExtrude","SWEPT_FACE",FACE,{"disambiguationData":[OSD([subQ0]),TDD([subQ1])]})]}),makeQuery(id+"F28.opExtrude","SWEPT_FACE",FACE,{"disambiguationData":[OSD([subQ0]),TDD([makeQuery(id+"F27.opExtrude","CAP_EDGE",EDGE,{"disambiguationData":[OSD([subQ0]),TDD([makeQuery(id+"F22.boolean.opBoolean","COPY",EDGE,{"derivedFrom":makeQuery(id+"F22.opExtrude","CAP_EDGE",EDGE,{"disambiguationData":[OSD([subQ0]),TDD([subQ1])],"isStart":false})})])],"isStart":false})])]})]});}
            var Q5;
            {var subQ0=sQuery(id+"F15.wireOp",EDGE,"E6.top");var subQ1=makeQuery(id+"F17.opExtrude","CAP_EDGE",EDGE,{"disambiguationData":[OSD([subQ0]),TDD([makeQuery(id+"F16.opExtrude","CAP_EDGE",EDGE,{"disambiguationData":[OSD([subQ0])],"isStart":true})])],"isStart":false});var subQ2=sQuery(id+"F10.wireOp",EDGE,"E2.right");var subQ3=sQuery(id+"F4.wireOp",EDGE,"E1.top");var subQ4=makeQuery(id+"F8.boolean.opBoolean","COPY",FACE,{"derivedFrom":makeQuery(id+"F8.opExtrude","CAP_FACE",FACE,{"disambiguationData":[OSD([subQ3])],"isStart":false})});var subQ5=sQuery(id+"F4.wireOp",EDGE,"E1.right");var subQ7=sQuery(id+"F4.wireOp",EDGE,"E1.bottom");Q5=makeQuery(id+"F40.boolean.opBoolean","MERGE",FACE,{"derivedFrom":[makeQuery(id+"F38.boolean.opBoolean","MERGE",FACE,{"derivedFrom":[makeQuery(id+"F16.boolean.opBoolean","SPLIT",FACE,{"disambiguationData":[TD([subQ4])],"derivedFrom":makeQuery(id+"F13.boolean.opBoolean","MERGE",FACE,{"derivedFrom":[makeQuery(id+"F11.boolean.opBoolean","SPLIT",FACE,{"disambiguationData":[TD([makeQuery(id+"F11.opExtrude","SWEPT_FACE",FACE,{"disambiguationData":[OSD([subQ2])]})])],"derivedFrom":makeQuery(id+"F8.boolean.opBoolean","MERGE",FACE,{"derivedFrom":[makeQuery(id+"F6.boolean.opBoolean","MERGE",FACE,{"derivedFrom":[makeQuery(id+"F5.boolean.opBoolean","COPY",FACE,{"derivedFrom":makeQuery(id+"F5.opExtrude","CAP_FACE",FACE,{"disambiguationData":[OSD([subQ7,subQ3,sQuery(id+"F4.wireOp",EDGE,"E1.left"),subQ5])],"isStart":false})}),makeQuery(id+"F6.opExtrude","SWEPT_FACE",FACE,{"disambiguationData":[OSD([subQ7]),TDD([makeQuery(id+"F5.boolean.opBoolean","COPY",EDGE,{"derivedFrom":makeQuery(id+"F5.opExtrude","CAP_EDGE",EDGE,{"disambiguationData":[OSD([subQ7])],"isStart":false})})])]})]}),makeQuery(id+"F8.opExtrude","SWEPT_FACE",FACE,{"disambiguationData":[OSD([subQ3]),TDD([makeQuery(id+"F5.boolean.opBoolean","COPY",EDGE,{"derivedFrom":makeQuery(id+"F5.opExtrude","CAP_EDGE",EDGE,{"disambiguationData":[OSD([subQ3])],"isStart":false})})])]})]})}),makeQuery(id+"F13.opExtrude","SWEPT_FACE",FACE,{"disambiguationData":[OSD([subQ2]),TDD([makeQuery(id+"F11.opExtrude","CAP_EDGE",EDGE,{"disambiguationData":[OSD([subQ2])],"isStart":true})])]})]})}),makeQuery(id+"F38.opExtrude","SWEPT_FACE",FACE,{"disambiguationData":[OSD([subQ0]),TDD([subQ1])]})]}),makeQuery(id+"F40.opExtrude","SWEPT_FACE",FACE,{"disambiguationData":[OSD([subQ0]),TDD([makeQuery(id+"F38.boolean.opBoolean","COPY",EDGE,{"derivedFrom":makeQuery(id+"F38.opExtrude","CAP_EDGE",EDGE,{"disambiguationData":[OSD([subQ0]),TDD([subQ1])],"isStart":false})})])]})]});}
            extrude(context, id + "F41", {"entities" : qUnion([Q0, Q1, Q2, Q3, Q4, Q5]), "operationType" : NewBodyOperationType.REMOVE, "oppositeDirection" : true, "depth" : 11 * mm, "offsetDistance" : 25 * mm});
        }
        {
            var Q0;
            {var subQ0=sQuery(id+"F15.wireOp",EDGE,"E6.bottom");var subQ1=sQuery(id+"F15.wireOp",EDGE,"E5.top");var subQ2=sQuery(id+"F14.wireOp",EDGE,"E4.top");var subQ3=makeQuery(id+"F16.opExtrude","CAP_EDGE",EDGE,{"disambiguationData":[OSD([subQ2])],"isStart":false});var subQ4=makeQuery(id+"F22.boolean.opBoolean","COPY",EDGE,{"derivedFrom":makeQuery(id+"F22.opExtrude","CAP_EDGE",EDGE,{"disambiguationData":[OSD([subQ2]),TDD([makeQuery(id+"F17.opExtrude","CAP_EDGE",EDGE,{"disambiguationData":[OSD([subQ2]),TDD([subQ3])],"isStart":false})])],"isStart":false})});var subQ5=sQuery(id+"F14.wireOp",EDGE,"E3.bottom");var subQ6=makeQuery(id+"F20.boolean.opBoolean","COPY",EDGE,{"derivedFrom":makeQuery(id+"F20.opExtrude","CAP_EDGE",EDGE,{"disambiguationData":[OSD([subQ5]),TDD([makeQuery(id+"F16.opExtrude","CAP_EDGE",EDGE,{"disambiguationData":[OSD([subQ5])],"isStart":false})])],"isStart":false})});var subQ7=makeQuery(id+"F23.opExtrude","CAP_EDGE",EDGE,{"disambiguationData":[OSD([subQ5]),TDD([subQ6])],"isStart":false});var subQ8=sQuery(id+"F14.wireOp",EDGE,"E3.top");var subQ9=makeQuery(id+"F16.opExtrude","CAP_EDGE",EDGE,{"disambiguationData":[OSD([subQ8])],"isStart":false});var subQ10=sQuery(id+"F14.wireOp",EDGE,"E4.bottom");var subQ11=sQuery(id+"F15.wireOp",EDGE,"E6.top");var subQ12=sQuery(id+"F4.wireOp",EDGE,"E1.left");var subQ13=sQuery(id+"F4.wireOp",EDGE,"E1.top");var subQ14=sQuery(id+"F4.wireOp",EDGE,"E1.bottom");var subQ15=sQuery(id+"F4.wireOp",EDGE,"E1.right");var subQ16=sQuery(id+"F0.wireOp",EDGE,"E0.left");var subQ17=sQuery(id+"F0.wireOp",EDGE,"E0.bottom");Q0=makeQuery(id+"F39.boolean.opBoolean","MERGE",FACE,{"derivedFrom":[makeQuery(id+"F36.boolean.opBoolean","MERGE",FACE,{"derivedFrom":[makeQuery(id+"F33.boolean.opBoolean","MERGE",FACE,{"derivedFrom":[makeQuery(id+"F31.boolean.opBoolean","MERGE",FACE,{"derivedFrom":[makeQuery(id+"F29.boolean.opBoolean","MERGE",FACE,{"derivedFrom":[makeQuery(id+"F27.boolean.opBoolean","MERGE",FACE,{"derivedFrom":[makeQuery(id+"F25.boolean.opBoolean","MERGE",FACE,{"derivedFrom":[makeQuery(id+"F23.boolean.opBoolean","MERGE",FACE,{"derivedFrom":[makeQuery(id+"F21.boolean.opBoolean","MERGE",FACE,{"derivedFrom":[makeQuery(id+"F19.boolean.opBoolean","MERGE",FACE,{"derivedFrom":[makeQuery(id+"F17.boolean.opBoolean","MERGE",FACE,{"derivedFrom":[makeQuery(id+"F16.boolean.opBoolean","MERGE",FACE,{"derivedFrom":[makeQuery(id+"F11.boolean.opBoolean","MERGE",FACE,{"derivedFrom":[makeQuery(id+"F9.boolean.opBoolean","MERGE",FACE,{"derivedFrom":[makeQuery(id+"F7.boolean.opBoolean","MERGE",FACE,{"derivedFrom":[makeQuery(id+"F3.boolean.opBoolean","MERGE",FACE,{"derivedFrom":[makeQuery(id+"F2.boolean.opBoolean","MERGE",FACE,{"derivedFrom":[makeQuery(id+"F1.opExtrude","CAP_FACE",FACE,{"disambiguationData":[OSD([subQ17,sQuery(id+"F0.wireOp",EDGE,"E0.top"),subQ16,sQuery(id+"F0.wireOp",EDGE,"E0.right")])],"isStart":false}),makeQuery(id+"F2.opExtrude","SWEPT_FACE",FACE,{"disambiguationData":[OSD([subQ16]),TDD([makeQuery(id+"F1.opExtrude","CAP_EDGE",EDGE,{"disambiguationData":[OSD([subQ16])],"isStart":false})])]})]}),makeQuery(id+"F3.opExtrude","SWEPT_FACE",FACE,{"disambiguationData":[OSD([subQ17,subQ16]),TDD([makeQuery(id+"F2.boolean.opBoolean","MERGE",EDGE,{"derivedFrom":[makeQuery(id+"F1.opExtrude","CAP_EDGE",EDGE,{"disambiguationData":[OSD([subQ17])],"isStart":false}),makeQuery(id+"F2.opExtrude","SWEPT_EDGE",EDGE,{"disambiguationData":[OSD([subQ17,subQ16]),TDD([makeQuery(id+"F1.opExtrude","CAP_VERTEX",VERTEX,{"disambiguationData":[OSD([subQ17,subQ16])],"isStart":false})])]})]})])]})]}),makeQuery(id+"F7.opExtrude","SWEPT_FACE",FACE,{"disambiguationData":[OSD([subQ14,subQ15]),TDD([makeQuery(id+"F6.boolean.opBoolean","MERGE",EDGE,{"derivedFrom":[makeQuery(id+"F5.boolean.opBoolean","COPY",EDGE,{"derivedFrom":makeQuery(id+"F5.opExtrude","CAP_EDGE",EDGE,{"disambiguationData":[OSD([subQ15])],"isStart":true})}),makeQuery(id+"F6.opExtrude","SWEPT_EDGE",EDGE,{"disambiguationData":[OSD([subQ14,subQ15]),TDD([makeQuery(id+"F5.boolean.opBoolean","COPY",VERTEX,{"derivedFrom":makeQuery(id+"F5.opExtrude","CAP_VERTEX",VERTEX,{"disambiguationData":[OSD([subQ14,subQ15])],"isStart":true})})])]})]})])]})]}),makeQuery(id+"F9.opExtrude","SWEPT_FACE",FACE,{"disambiguationData":[OSD([subQ14,subQ13,subQ12]),TDD([makeQuery(id+"F8.boolean.opBoolean","MERGE",EDGE,{"derivedFrom":[makeQuery(id+"F6.boolean.opBoolean","MERGE",EDGE,{"derivedFrom":[makeQuery(id+"F5.boolean.opBoolean","COPY",EDGE,{"derivedFrom":makeQuery(id+"F5.opExtrude","CAP_EDGE",EDGE,{"disambiguationData":[OSD([subQ12])],"isStart":true})}),makeQuery(id+"F6.opExtrude","SWEPT_EDGE",EDGE,{"disambiguationData":[OSD([subQ14,subQ12]),TDD([makeQuery(id+"F5.boolean.opBoolean","COPY",VERTEX,{"derivedFrom":makeQuery(id+"F5.opExtrude","CAP_VERTEX",VERTEX,{"disambiguationData":[OSD([subQ14,subQ12])],"isStart":true})})])]})]}),makeQuery(id+"F8.opExtrude","SWEPT_EDGE",EDGE,{"disambiguationData":[OSD([subQ13,subQ12]),TDD([makeQuery(id+"F5.boolean.opBoolean","COPY",VERTEX,{"derivedFrom":makeQuery(id+"F5.opExtrude","CAP_VERTEX",VERTEX,{"disambiguationData":[OSD([subQ13,subQ12])],"isStart":true})})])]})]})])]})]}),makeQuery(id+"F11.opExtrude","CAP_FACE",FACE,{"disambiguationData":[OSD([sQuery(id+"F10.wireOp",EDGE,"E2.bottom"),sQuery(id+"F10.wireOp",EDGE,"E2.top"),sQuery(id+"F10.wireOp",EDGE,"E2.left"),sQuery(id+"F10.wireOp",EDGE,"E2.right")])],"isStart":false})]}),makeQuery(id+"F16.opExtrude","CAP_FACE",FACE,{"disambiguationData":[OSD([subQ5,subQ8,sQuery(id+"F14.wireOp",EDGE,"E3.left"),sQuery(id+"F14.wireOp",EDGE,"E3.right")])],"isStart":false}),makeQuery(id+"F16.opExtrude","CAP_FACE",FACE,{"disambiguationData":[OSD([subQ10,subQ2,sQuery(id+"F14.wireOp",EDGE,"E4.left"),sQuery(id+"F14.wireOp",EDGE,"E4.right")])],"isStart":false}),makeQuery(id+"F16.opExtrude","CAP_FACE",FACE,{"disambiguationData":[OSD([sQuery(id+"F15.wireOp",EDGE,"E5.bottom"),subQ1,sQuery(id+"F15.wireOp",EDGE,"E5.left"),sQuery(id+"F15.wireOp",EDGE,"E5.right")])],"isStart":false}),makeQuery(id+"F16.opExtrude","CAP_FACE",FACE,{"disambiguationData":[OSD([subQ0,subQ11,sQuery(id+"F15.wireOp",EDGE,"E6.left"),sQuery(id+"F15.wireOp",EDGE,"E6.right")])],"isStart":false})]}),makeQuery(id+"F17.opExtrude","SWEPT_FACE",FACE,{"disambiguationData":[OSD([subQ2]),TDD([subQ3])]}),makeQuery(id+"F17.opExtrude","SWEPT_FACE",FACE,{"disambiguationData":[OSD([subQ11]),TDD([makeQuery(id+"F16.opExtrude","CAP_EDGE",EDGE,{"disambiguationData":[OSD([subQ11])],"isStart":false})])]})]}),makeQuery(id+"F19.opExtrude","SWEPT_FACE",FACE,{"disambiguationData":[OSD([subQ8]),TDD([subQ9])]})]}),makeQuery(id+"F21.opExtrude","SWEPT_FACE",FACE,{"disambiguationData":[OSD([subQ10]),TDD([makeQuery(id+"F18.boolean.opBoolean","COPY",EDGE,{"derivedFrom":makeQuery(id+"F18.opExtrude","CAP_EDGE",EDGE,{"disambiguationData":[OSD([subQ10]),TDD([makeQuery(id+"F16.opExtrude","CAP_EDGE",EDGE,{"disambiguationData":[OSD([subQ10])],"isStart":false})])],"isStart":false})})])]})]}),makeQuery(id+"F23.opExtrude","SWEPT_FACE",FACE,{"disambiguationData":[OSD([subQ5]),TDD([subQ6])]})]}),makeQuery(id+"F25.opExtrude","SWEPT_FACE",FACE,{"disambiguationData":[OSD([subQ5]),TDD([subQ7])]})]}),makeQuery(id+"F27.opExtrude","SWEPT_FACE",FACE,{"disambiguationData":[OSD([subQ2]),TDD([subQ4])]})]}),makeQuery(id+"F29.opExtrude","SWEPT_FACE",FACE,{"disambiguationData":[OSD([subQ8]),TDD([makeQuery(id+"F26.boolean.opBoolean","COPY",EDGE,{"derivedFrom":makeQuery(id+"F26.opExtrude","CAP_EDGE",EDGE,{"disambiguationData":[OSD([subQ8]),TDD([makeQuery(id+"F24.boolean.opBoolean","COPY",EDGE,{"derivedFrom":makeQuery(id+"F24.opExtrude","CAP_EDGE",EDGE,{"disambiguationData":[OSD([subQ8]),TDD([makeQuery(id+"F19.opExtrude","CAP_EDGE",EDGE,{"disambiguationData":[OSD([subQ8]),TDD([subQ9])],"isStart":false})])],"isStart":false})})])],"isStart":false})})])]})]}),makeQuery(id+"F31.opExtrude","SWEPT_FACE",FACE,{"disambiguationData":[OSD([subQ5]),TDD([makeQuery(id+"F30.boolean.opBoolean","COPY",EDGE,{"derivedFrom":makeQuery(id+"F30.opExtrude","CAP_EDGE",EDGE,{"disambiguationData":[OSD([subQ5]),TDD([makeQuery(id+"F25.opExtrude","CAP_EDGE",EDGE,{"disambiguationData":[OSD([subQ5]),TDD([subQ7])],"isStart":false})])],"isStart":false})})])]})]}),makeQuery(id+"F33.opExtrude","SWEPT_FACE",FACE,{"disambiguationData":[OSD([subQ2]),TDD([makeQuery(id+"F28.boolean.opBoolean","COPY",EDGE,{"derivedFrom":makeQuery(id+"F28.opExtrude","CAP_EDGE",EDGE,{"disambiguationData":[OSD([subQ2]),TDD([makeQuery(id+"F27.opExtrude","CAP_EDGE",EDGE,{"disambiguationData":[OSD([subQ2]),TDD([subQ4])],"isStart":false})])],"isStart":false})})])]})]}),makeQuery(id+"F36.opExtrude","SWEPT_FACE",FACE,{"disambiguationData":[OSD([subQ1]),TDD([makeQuery(id+"F35.boolean.opBoolean","COPY",EDGE,{"derivedFrom":makeQuery(id+"F35.opExtrude","CAP_EDGE",EDGE,{"disambiguationData":[OSD([subQ1]),TDD([makeQuery(id+"F16.opExtrude","CAP_EDGE",EDGE,{"disambiguationData":[OSD([subQ1])],"isStart":false})])],"isStart":false})})])]})]}),makeQuery(id+"F39.opExtrude","SWEPT_FACE",FACE,{"disambiguationData":[OSD([subQ0]),TDD([makeQuery(id+"F18.boolean.opBoolean","COPY",EDGE,{"derivedFrom":makeQuery(id+"F18.opExtrude","CAP_EDGE",EDGE,{"disambiguationData":[OSD([subQ0]),TDD([makeQuery(id+"F16.opExtrude","CAP_EDGE",EDGE,{"disambiguationData":[OSD([subQ0])],"isStart":false})])],"isStart":false})})])]})]});}
            fillet(context, id + "F42", {"entities" : qUnion([Q0]), "radius" : 3 * mm, "tangentPropagation" : true, "allowEdgeOverflow" : false});
        }
    });
